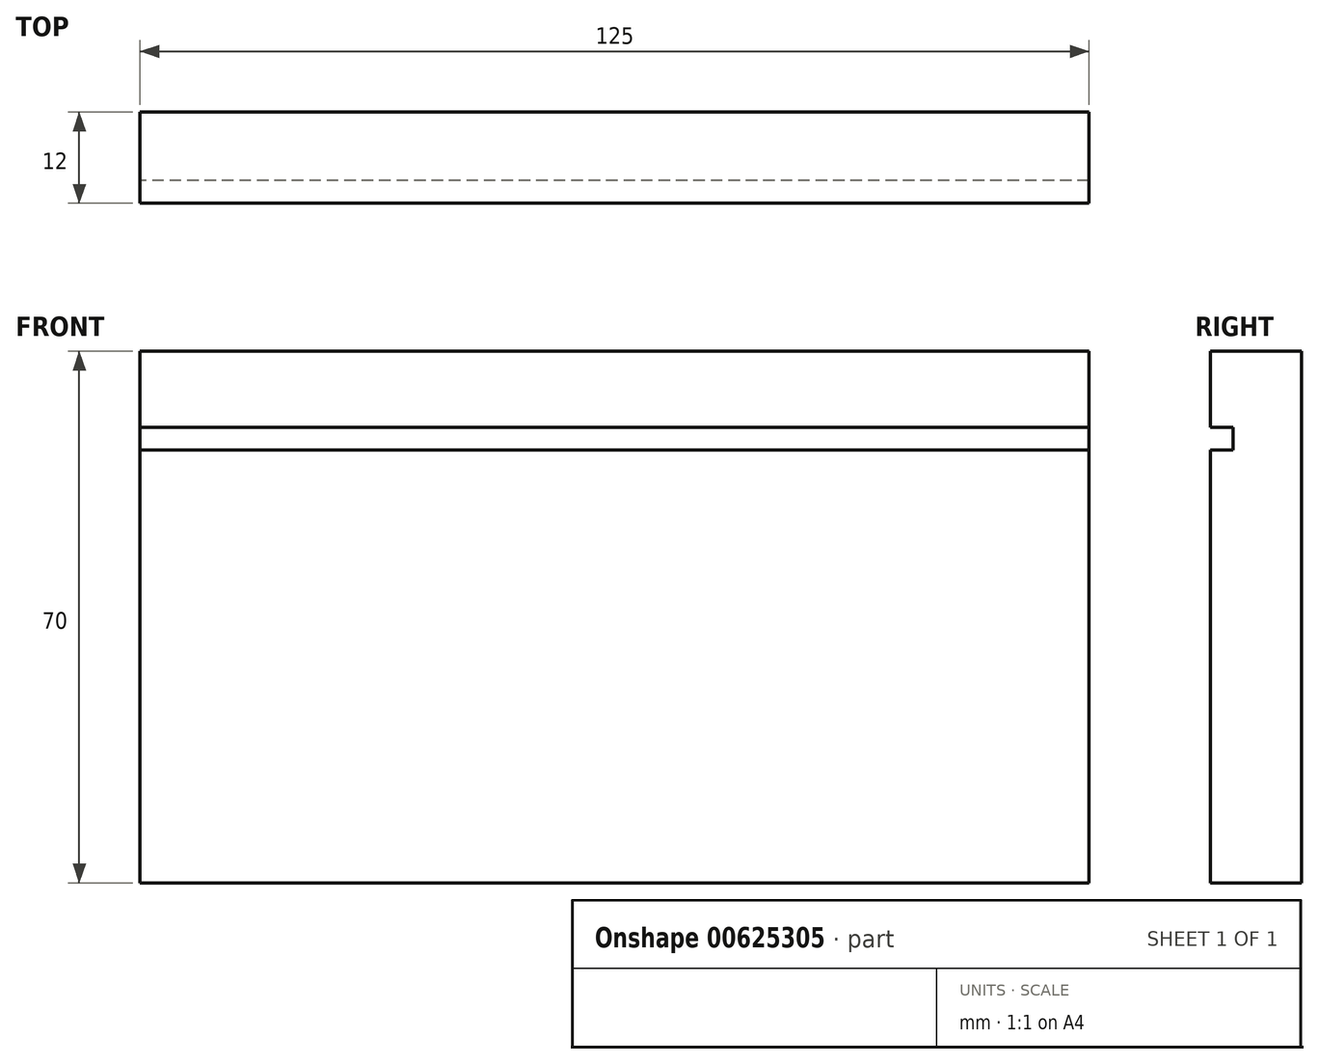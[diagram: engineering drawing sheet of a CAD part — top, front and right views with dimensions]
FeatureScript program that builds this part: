
annotation { "Feature Type Name" : "Feature", "Feature Type Description" : "" }
export const myFeature = defineFeature(function(context is Context, id is Id, definition is map)
    precondition{}
    {
        {
            var Q0;
            Q0=qCreatedBy(makeId("Right.planeOp"),FACE);
            var sketch = newSketch(context, id + "F0", { "sketchPlane" : qUnion([Q0])});
            skLineSegment(sketch, "E0", {"start": v(0, 0) * mm, "end": v(12, 0) * mm});
            skLineSegment(sketch, "E1", {"start": v(12, 0) * mm, "end": v(12, 70) * mm});
            skLineSegment(sketch, "E2", {"start": v(12, 70) * mm, "end": v(0, 70) * mm});
            skLineSegment(sketch, "E3", {"start": v(0, 70) * mm, "end": v(0, 60) * mm});
            skLineSegment(sketch, "E4", {"start": v(0, 60) * mm, "end": v(3, 60) * mm});
            skLineSegment(sketch, "E5", {"start": v(3, 60) * mm, "end": v(3, 57) * mm});
            skLineSegment(sketch, "E6", {"start": v(3, 57) * mm, "end": v(0, 57) * mm});
            skLineSegment(sketch, "E7", {"start": v(0, 57) * mm, "end": v(0, 0) * mm});
            skSolve(sketch);
        }
        {
            var Q0;
            Q0=makeQuery(id+"F0.imprint","IMPRINT",FACE,{"disambiguationData":[TD([[makeQuery(id+"F0.imprint","IMPRINT",EDGE,{"derivedFrom":sQuery(id+"F0.wireOp",EDGE,"E0")}),1.0]])]});
            extrude(context, id + "F1", {"entities" : qUnion([Q0]), "depth" : 25 * mm, "offsetDistance" : 25 * mm});
        }
        {
            var Q0;
            Q0=makeQuery(id+"F1.opExtrude","CAP_FACE",FACE,{"disambiguationData":[OSD([sQuery(id+"F0.wireOp",EDGE,"E0"),sQuery(id+"F0.wireOp",EDGE,"E1"),sQuery(id+"F0.wireOp",EDGE,"E2"),sQuery(id+"F0.wireOp",EDGE,"E3"),sQuery(id+"F0.wireOp",EDGE,"E4"),sQuery(id+"F0.wireOp",EDGE,"E5"),sQuery(id+"F0.wireOp",EDGE,"E6"),sQuery(id+"F0.wireOp",EDGE,"E7")])],"isStart":false});
            extrude(context, id + "F2", {"entities" : qUnion([Q0]), "operationType" : NewBodyOperationType.ADD, "depth" : 25 * mm, "offsetDistance" : 25 * mm});
        }
        {
            var Q0;
            Q0=makeQuery(id+"F2.opExtrude","CAP_FACE",FACE,{"disambiguationData":[OSD([sQuery(id+"F0.wireOp",EDGE,"E0"),sQuery(id+"F0.wireOp",EDGE,"E1"),sQuery(id+"F0.wireOp",EDGE,"E2"),sQuery(id+"F0.wireOp",EDGE,"E3"),sQuery(id+"F0.wireOp",EDGE,"E4"),sQuery(id+"F0.wireOp",EDGE,"E5"),sQuery(id+"F0.wireOp",EDGE,"E6"),sQuery(id+"F0.wireOp",EDGE,"E7")])],"isStart":false});
            extrude(context, id + "F3", {"entities" : qUnion([Q0]), "operationType" : NewBodyOperationType.ADD, "depth" : 25 * mm, "offsetDistance" : 25 * mm});
        }
        {
            var Q0;
            Q0=makeQuery(id+"F3.opExtrude","CAP_FACE",FACE,{"disambiguationData":[OSD([sQuery(id+"F0.wireOp",EDGE,"E0"),sQuery(id+"F0.wireOp",EDGE,"E1"),sQuery(id+"F0.wireOp",EDGE,"E2"),sQuery(id+"F0.wireOp",EDGE,"E3"),sQuery(id+"F0.wireOp",EDGE,"E4"),sQuery(id+"F0.wireOp",EDGE,"E5"),sQuery(id+"F0.wireOp",EDGE,"E6"),sQuery(id+"F0.wireOp",EDGE,"E7")])],"isStart":false});
            extrude(context, id + "F4", {"entities" : qUnion([Q0]), "operationType" : NewBodyOperationType.ADD, "depth" : 25 * mm, "offsetDistance" : 25 * mm});
        }
        {
            var Q0;
            Q0=makeQuery(id+"F4.opExtrude","CAP_FACE",FACE,{"disambiguationData":[OSD([sQuery(id+"F0.wireOp",EDGE,"E0"),sQuery(id+"F0.wireOp",EDGE,"E1"),sQuery(id+"F0.wireOp",EDGE,"E2"),sQuery(id+"F0.wireOp",EDGE,"E3"),sQuery(id+"F0.wireOp",EDGE,"E4"),sQuery(id+"F0.wireOp",EDGE,"E5"),sQuery(id+"F0.wireOp",EDGE,"E6"),sQuery(id+"F0.wireOp",EDGE,"E7")])],"isStart":false});
            extrude(context, id + "F5", {"entities" : qUnion([Q0]), "operationType" : NewBodyOperationType.ADD, "depth" : 25 * mm, "offsetDistance" : 25 * mm});
        }
    });
